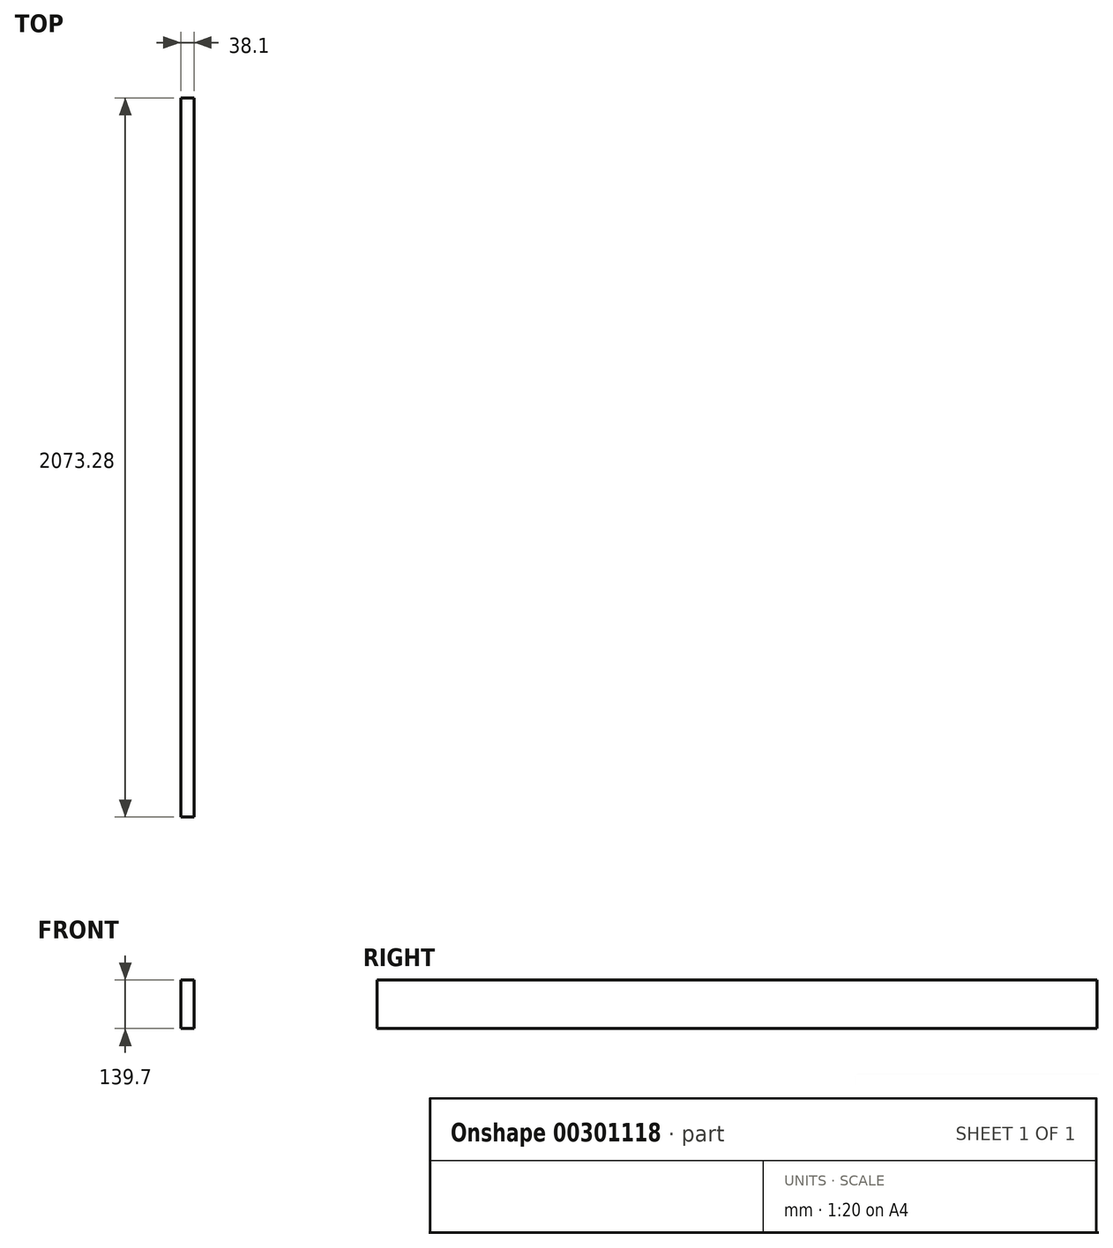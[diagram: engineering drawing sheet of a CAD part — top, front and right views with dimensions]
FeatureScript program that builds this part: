
annotation { "Feature Type Name" : "Feature", "Feature Type Description" : "" }
export const myFeature = defineFeature(function(context is Context, id is Id, definition is map)
    precondition{}
    {
        {
            var Q0;
            Q0=qCreatedBy(makeId("Front.planeOp"),FACE);
            var sketch = newSketch(context, id + "F0", { "sketchPlane" : qUnion([Q0])});
            skLineSegment(sketch, "E0.bottom", {"start": v(0, 0) * mm, "end": v(38.1, 0) * mm});
            skLineSegment(sketch, "E0.top", {"start": v(0, 139.7) * mm, "end": v(38.1, 139.7) * mm});
            skLineSegment(sketch, "E0.left", {"start": v(0, 0) * mm, "end": v(0, 139.7) * mm});
            skLineSegment(sketch, "E0.right", {"start": v(38.1, 0) * mm, "end": v(38.1, 139.7) * mm});
            skSolve(sketch);
        }
        {
            var Q0;
            Q0 = qSketchRegion(id + "F0", true);
            extrude(context, id + "F1", {"entities" : qUnion([Q0]), "oppositeDirection" : true, "depth" : 2073.28 * mm});
        }
    });
